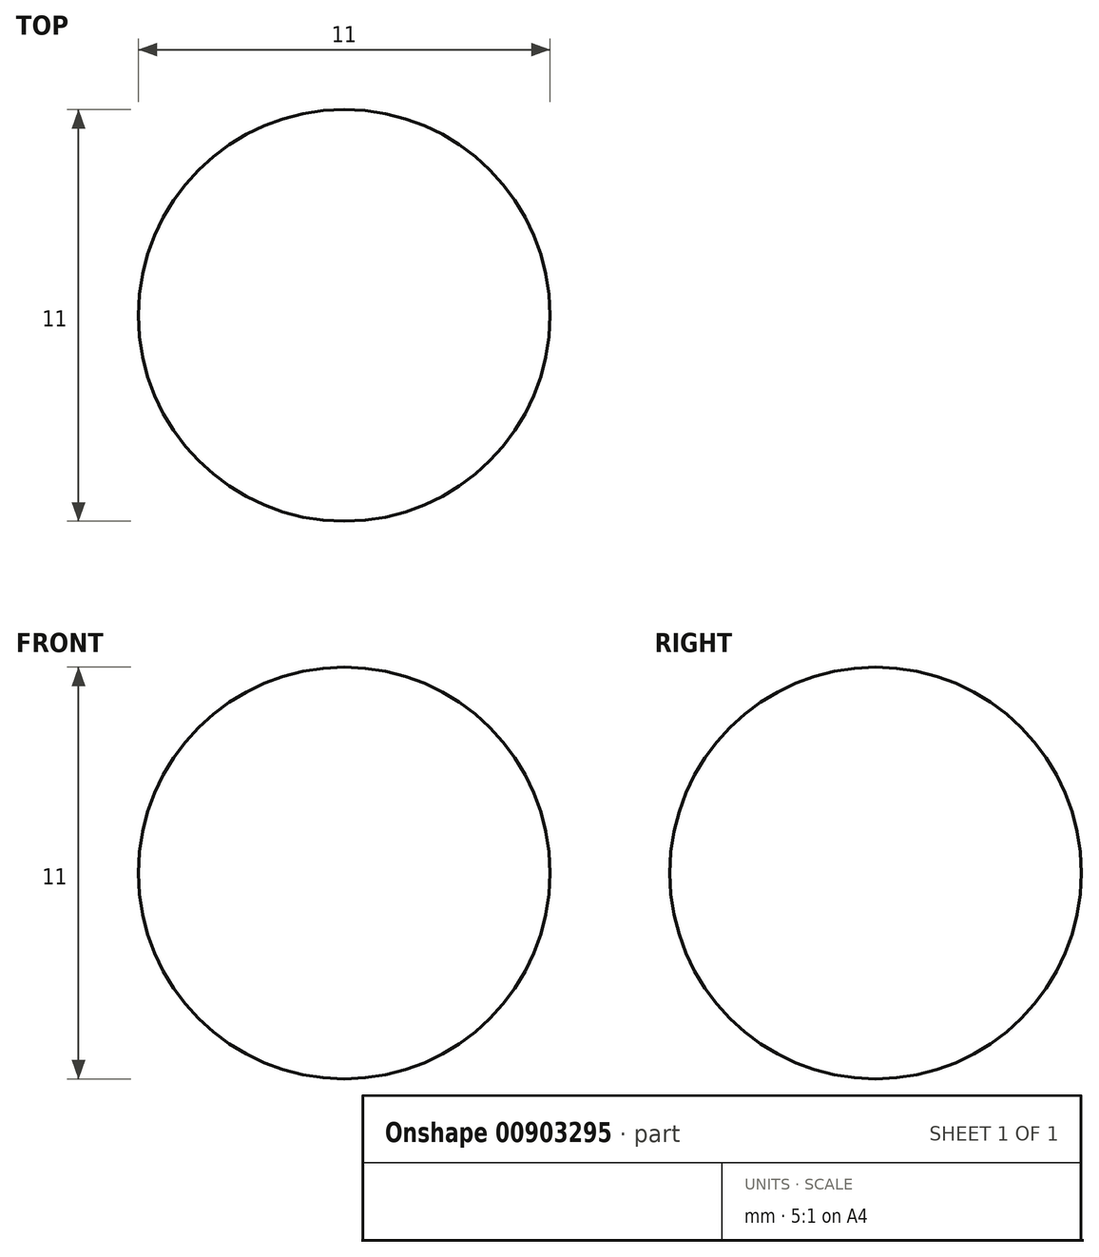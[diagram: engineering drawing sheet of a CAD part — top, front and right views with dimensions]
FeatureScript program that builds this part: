
annotation { "Feature Type Name" : "Feature", "Feature Type Description" : "" }
export const myFeature = defineFeature(function(context is Context, id is Id, definition is map)
    precondition{}
    {
        {
            var Q0;
            Q0=qCreatedBy(makeId("Front.planeOp"),FACE);
            var sketch = newSketch(context, id + "F0", { "sketchPlane" : qUnion([Q0])});
            skLineSegment(sketch, "E0", {"start": v(0, 5.5) * mm, "end": v(0, -5.5) * mm});
            skArc(sketch, "E1", {"start": v(0, -5.5) * mm, "mid": v(5.5, 0) * mm, "end": v(0, 5.5) * mm});
            skLineSegment(sketch, "E2", {"start": v(5.5, 0) * mm, "end": v(0, 0) * mm, "construction": true});
            skLineSegment(sketch, "E3", {"start": v(0, 6.4) * mm, "end": v(0, -6.85) * mm, "construction": true});
            skSolve(sketch);
        }
        {
            var Q0;
            Q0=makeQuery(id+"F0.imprint","IMPRINT",FACE,{"disambiguationData":[TD([[makeQuery(id+"F0.imprint","IMPRINT",EDGE,{"derivedFrom":sQuery(id+"F0.wireOp",EDGE,"E0")}),1.0]])]});
            var Q1;
            Q1=sQuery(id+"F0.wireOp",EDGE,"E3");
            revolve(context, id + "F1", {"surfaceOperationType" : NewSurfaceOperationType.NEW, "entities" : qUnion([Q0]), "axis" : qUnion([Q1]), "revolveType" : RevolveType.FULL});
        }
    });
